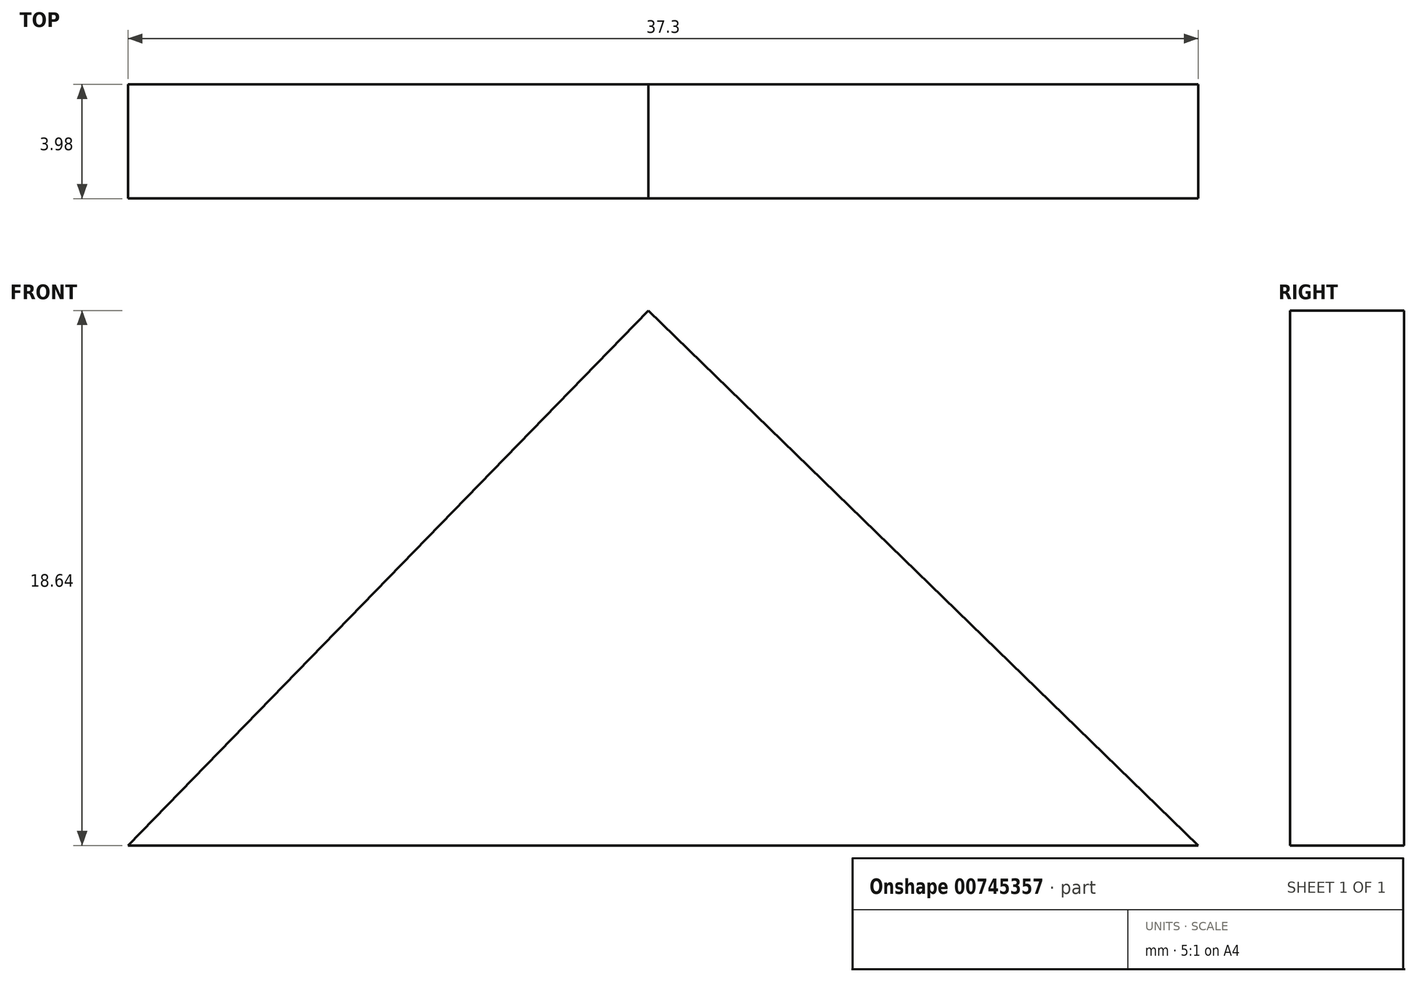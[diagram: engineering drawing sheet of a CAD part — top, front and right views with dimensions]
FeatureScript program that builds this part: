
annotation { "Feature Type Name" : "Feature", "Feature Type Description" : "" }
export const myFeature = defineFeature(function(context is Context, id is Id, definition is map)
    precondition{}
    {
        {
            var Q0;
            Q0=qCreatedBy(makeId("Front.planeOp"),FACE);
            var sketch = newSketch(context, id + "F0", { "sketchPlane" : qUnion([Q0])});
            skLineSegment(sketch, "E0", {"start": v(0, 0) * mm, "end": v(0, 18.64) * mm});
            skLineSegment(sketch, "E1", {"start": v(0, 18.64) * mm, "end": v(-18.14, 0) * mm});
            skLineSegment(sketch, "E2", {"start": v(0, 18.64) * mm, "end": v(19.16, 0) * mm});
            skLineSegment(sketch, "E3", {"start": v(-18.14, 0) * mm, "end": v(19.16, 0) * mm});
            skSolve(sketch);
        }
        {
            var Q0;
            {var subQ0=sQuery(id+"F0.wireOp",EDGE,"E0");Q0=makeQuery(id+"F0.imprint","IMPRINT",FACE,{"disambiguationData":[TD([[makeQuery(id+"F0.imprint","IMPRINT",EDGE,{"derivedFrom":subQ0}),-1.0]])]});}
            var Q1;
            {var subQ0=sQuery(id+"F0.wireOp",EDGE,"E0");Q1=makeQuery(id+"F0.imprint","IMPRINT",FACE,{"disambiguationData":[TD([[makeQuery(id+"F0.imprint","IMPRINT",EDGE,{"derivedFrom":subQ0}),1.0]])]});}
            extrude(context, id + "F1", {"entities" : qUnion([Q0, Q1]), "depth" : 3.98 * mm, "offsetDistance" : 25.4 * mm});
        }
    });
